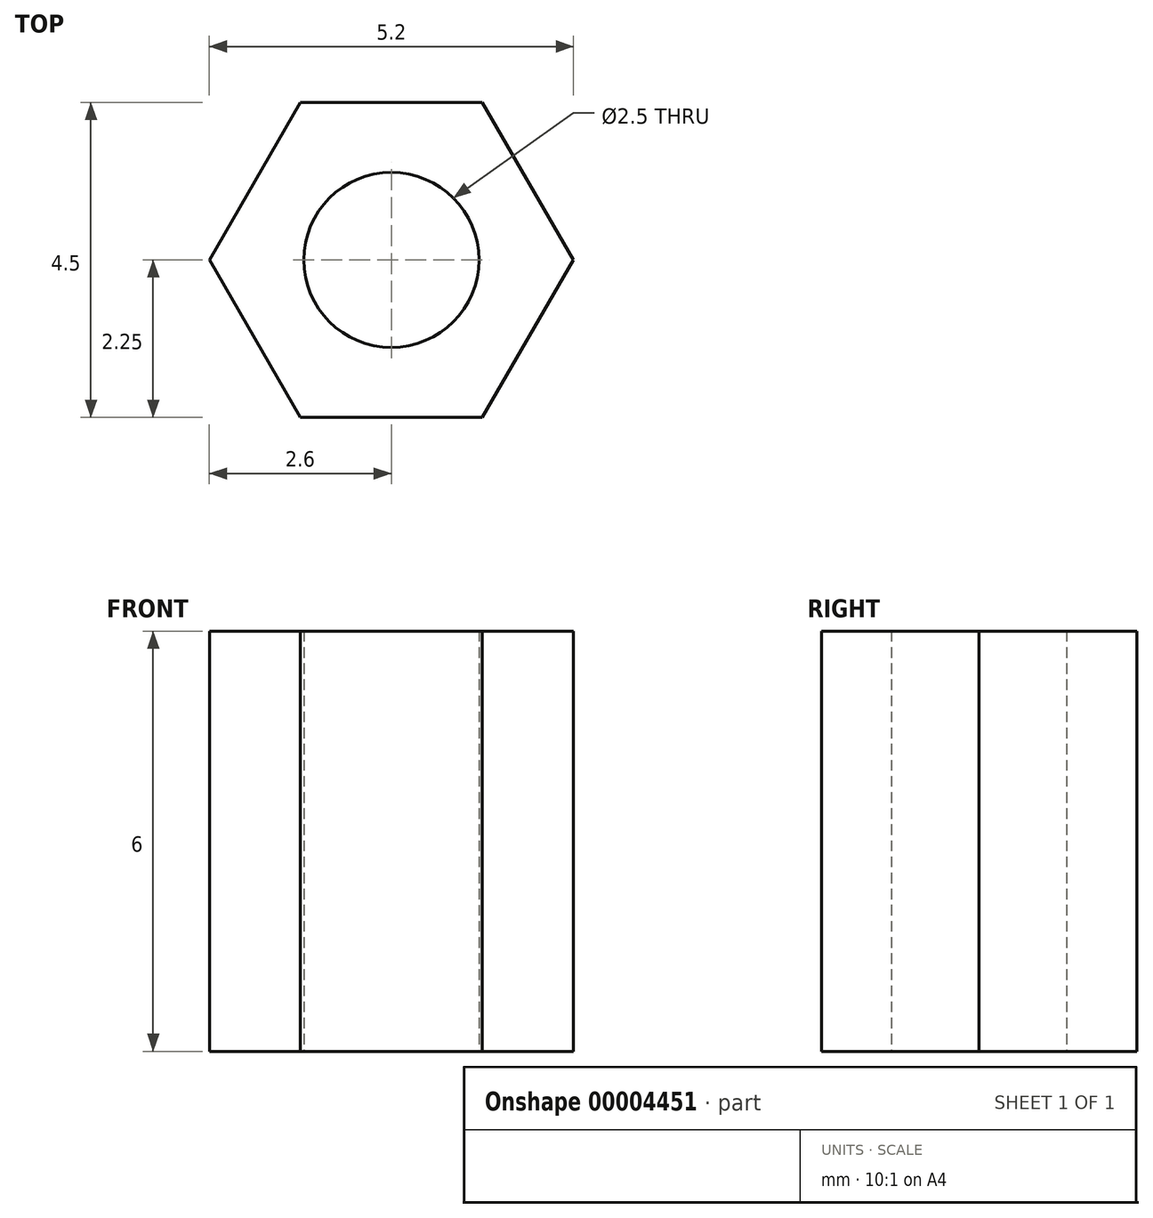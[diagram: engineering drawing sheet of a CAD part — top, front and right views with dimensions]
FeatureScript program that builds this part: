
annotation { "Feature Type Name" : "Feature", "Feature Type Description" : "" }
export const myFeature = defineFeature(function(context is Context, id is Id, definition is map)
    precondition{}
    {
        {
            var Q0;
            Q0=qCreatedBy(makeId("Top.planeOp"),FACE);
            var sketch = newSketch(context, id + "F0", { "sketchPlane" : qUnion([Q0])});
            skCircle(sketch, "E0", {"center": v(0, 0) * mm, "radius": 1.25 * mm});
            skCircle(sketch, "E1.cCircle", {"center": v(0, 0) * mm, "radius": 2.25 * mm, "construction": true});
            skLineSegment(sketch, "E1.0", {"start": v(-1.3, 2.25) * mm, "end": v(1.3, 2.25) * mm});
            skLineSegment(sketch, "E1.1", {"start": v(1.3, 2.25) * mm, "end": v(2.6, 0) * mm});
            skLineSegment(sketch, "E1.2", {"start": v(2.6, 0) * mm, "end": v(1.3, -2.25) * mm});
            skLineSegment(sketch, "E1.3", {"start": v(1.3, -2.25) * mm, "end": v(-1.3, -2.25) * mm});
            skLineSegment(sketch, "E1.4", {"start": v(-1.3, -2.25) * mm, "end": v(-2.6, 0) * mm});
            skLineSegment(sketch, "E1.5", {"start": v(-2.6, 0) * mm, "end": v(-1.3, 2.25) * mm});
            skPoint(sketch, "E1.0.midPoint", {"position": v(0, 2.25) * mm});
            skSolve(sketch);
        }
        {
            var Q0;
            Q0=makeQuery(id+"F0.imprint","IMPRINT",FACE,{"disambiguationData":[TD([[makeQuery(id+"F0.imprint","IMPRINT",EDGE,{"derivedFrom":sQuery(id+"F0.wireOp",EDGE,"E0")}),-1.0]])]});
            extrude(context, id + "F1", {"entities" : qUnion([Q0]), "depth" : 6 * mm});
        }
    });
